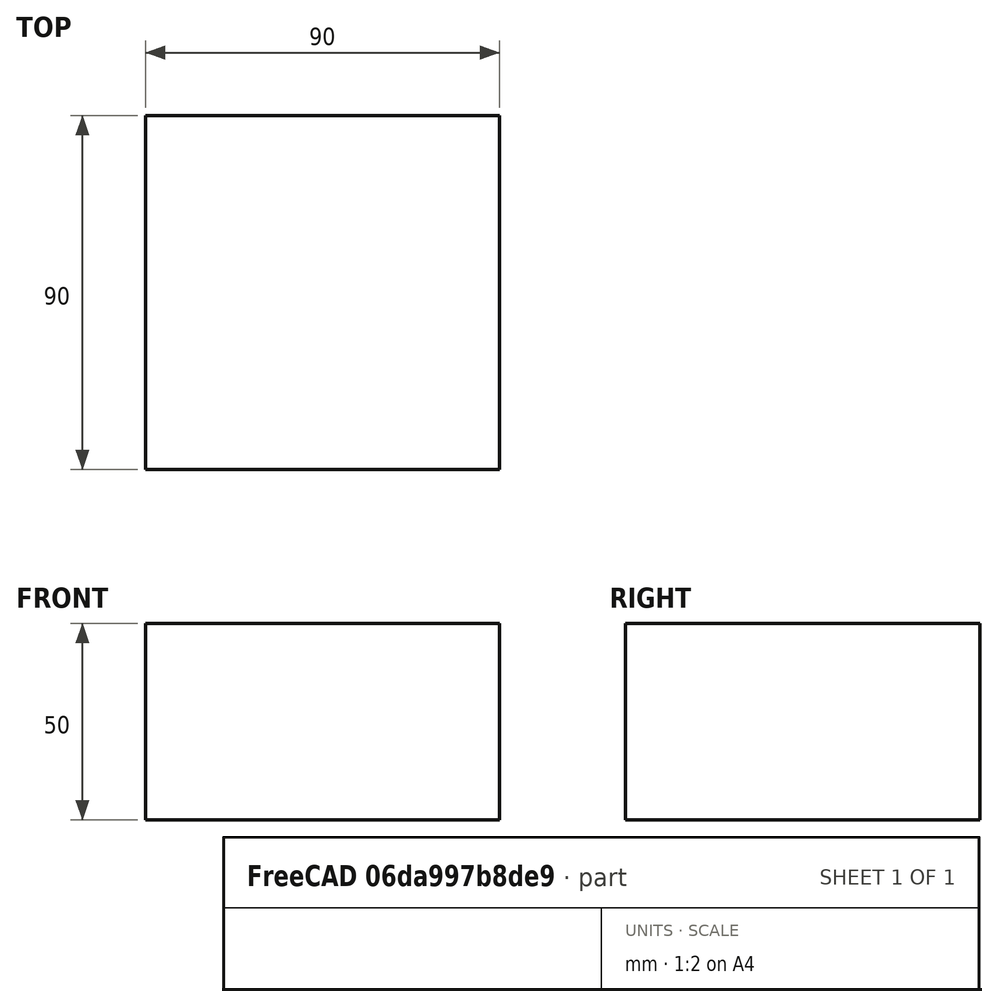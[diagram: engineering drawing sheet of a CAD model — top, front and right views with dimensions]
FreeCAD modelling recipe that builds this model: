
FCSTD DOCUMENT  (FreeCAD 0.15R4671 (Git))
Label: Square Bar 90 EN10059 S235JR
License: All rights reserved
LicenseURL: http://en.wikipedia.org/wiki/All_rights_reserved
objects: Sketcher::SketchObject×1, Part::Extrusion×1
note: 2 computed .brp shape members not serialized (recipe doc carries the construction recipe); baked Part::Feature solids carry a one-line shape summary decoded from their .brp

FEATURE [Sketcher::SketchObject] Sketch
  sketch-geometry (4):
    g0: LineSegment StartX=-45 StartY=-45 StartZ=0 EndX=45 EndY=-45 EndZ=0
    g1: LineSegment StartX=45 StartY=-45 StartZ=0 EndX=45 EndY=45 EndZ=0
    g2: LineSegment StartX=45 StartY=45 StartZ=0 EndX=-45 EndY=45 EndZ=0
    g3: LineSegment StartX=-45 StartY=45 StartZ=0 EndX=-45 EndY=-45 EndZ=0
  constraints (12):
    c: Coincident(g0,g1)
    c: Coincident(g1,g2)
    c: Coincident(g2,g3)
    c: Coincident(g3,g0)
    c: Horizontal(g0)
    c: Horizontal(g2)
    c: Vertical(g1)
    c: Vertical(g3)
    c: Symmetric(g1,g0,g-1)
    c: Symmetric(g2,g1,g-2)
    c: Equal(g1,g2)
    c: DistanceY(g1) = 90
FEATURE [Part::Extrusion] Extrude  label="Square Bar 90 EN10059 S235JR"
  Base = -> Sketch
  Dir = (0,0,50)
  Solid = true
